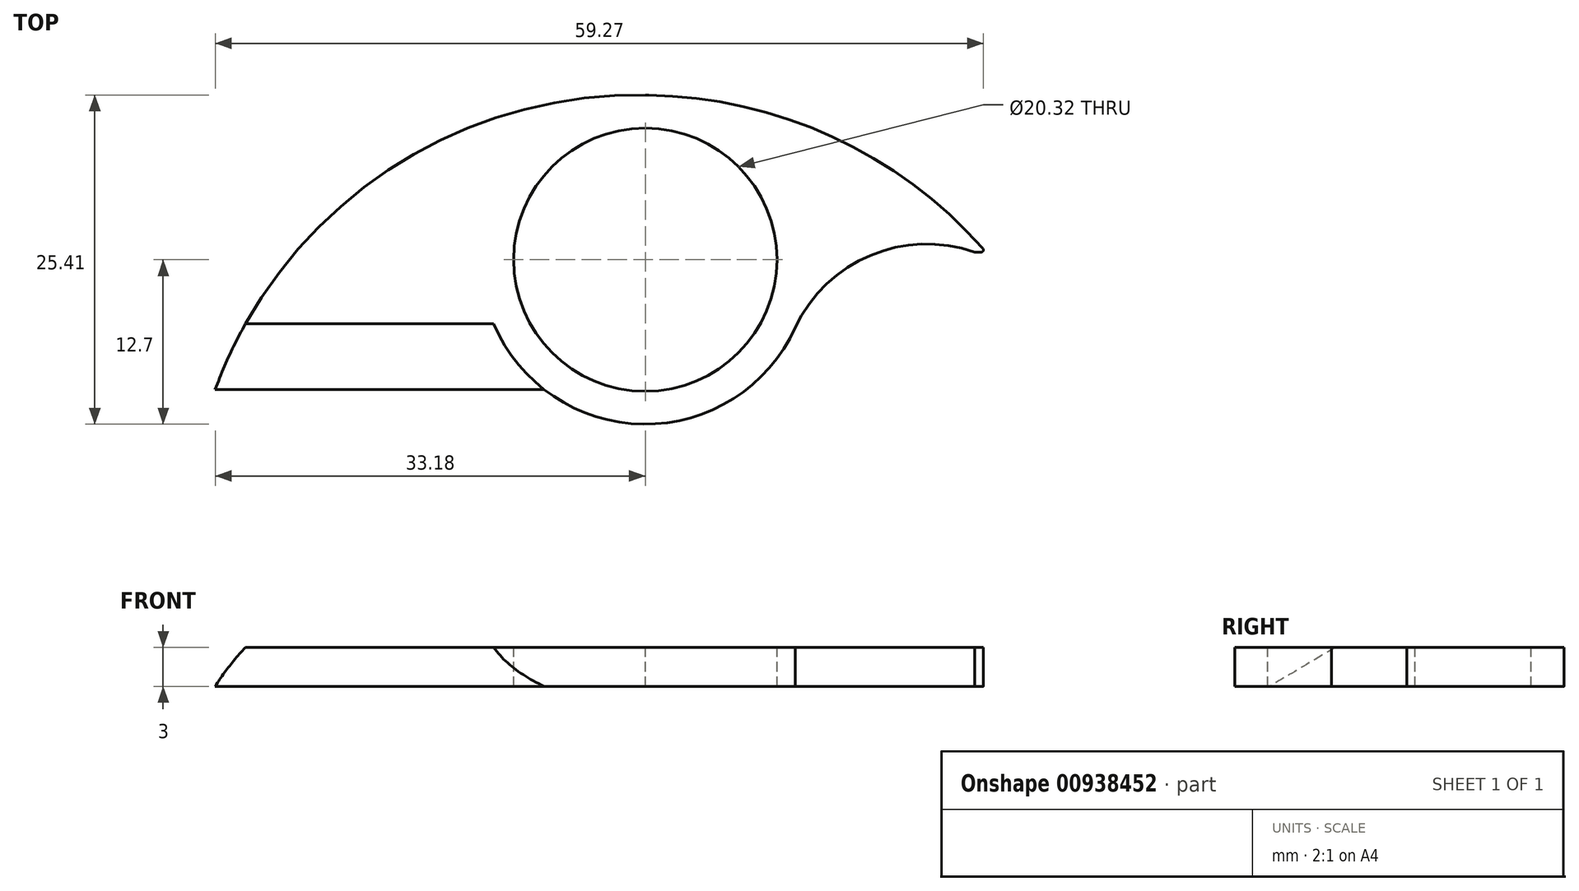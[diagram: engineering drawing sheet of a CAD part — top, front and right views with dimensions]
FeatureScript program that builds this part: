
annotation { "Feature Type Name" : "Feature", "Feature Type Description" : "" }
export const myFeature = defineFeature(function(context is Context, id is Id, definition is map)
    precondition{}
    {
        {
            var Q0;
            Q0=qCreatedBy(makeId("Top.planeOp"),FACE);
            var sketch = newSketch(context, id + "F0", { "sketchPlane" : qUnion([Q0])});
            skCircle(sketch, "E0", {"center": v(0, 0) * mm, "radius": 12.7 * mm});
            skSolve(sketch);
        }
        {
            var Q0;
            Q0 = qSketchRegion(id + "F0", true);
            extrude(context, id + "F1", {"entities" : qUnion([Q0]), "depth" : 3 * mm, "offsetDistance" : 25.4 * mm});
        }
        {
            var Q0;
            Q0=makeQuery(id+"F1.opExtrude","CAP_FACE",FACE,{"disambiguationData":[OSD([sQuery(id+"F0.wireOp",EDGE,"E0")])],"isStart":false});
            var sketch = newSketch(context, id + "F2", { "sketchPlane" : qUnion([Q0])});
            skLineSegment(sketch, "E1", {"start": v(-7.78, -10.04) * mm, "end": v(-33.18, -10.04) * mm});
            skArc(sketch, "E2", {"start": v(0, 12.7) * mm, "mid": v(-20.23, 6.65) * mm, "end": v(-33.18, -10.04) * mm});
            skSolve(sketch);
        }
        {
            var Q0;
            {var subQ0=makeQuery(id+"F1.opExtrude","CAP_EDGE",EDGE,{"disambiguationData":[OSD([sQuery(id+"F0.wireOp",EDGE,"E0")])],"isStart":false});var subQ1=makeQuery(id+"F2.imprint","INTERSECT",VERTEX,{"derivedFrom":[subQ0,sQuery(id+"F2.wireOp",EDGE,"E1")]});Q0=makeQuery(id+"F2.imprint","IMPRINT",FACE,{"disambiguationData":[TD([[makeQuery(id+"F2.imprint","IMPRINT",EDGE,{"disambiguationData":[TD([[subQ1,-1.0]])],"derivedFrom":subQ0}),1.0]])]});}
            var sketch = newSketch(context, id + "F3", { "sketchPlane" : qUnion([Q0])});
            skCircle(sketch, "E3.0", {"center": v(0, 0) * mm, "radius": 10.16 * mm});
            skSolve(sketch);
        }
        {
            var Q0;
            Q0=makeQuery(id+"F3.imprint","IMPRINT",FACE,{"disambiguationData":[TD([[makeQuery(id+"F3.imprint","IMPRINT",EDGE,{"derivedFrom":sQuery(id+"F3.wireOp",EDGE,"E3.0")}),1.0]])]});
            extrude(context, id + "F4", {"entities" : qUnion([Q0]), "operationType" : NewBodyOperationType.REMOVE, "oppositeDirection" : true, "depth" : 18.29 * mm, "offsetDistance" : 25.4 * mm});
        }
        {
            var Q0;
            {var subQ0=sQuery(id+"F2.wireOp",EDGE,"E1");Q0=makeQuery(id+"F2.imprint","IMPRINT",FACE,{"disambiguationData":[TD([[makeQuery(id+"F2.imprint","IMPRINT",EDGE,{"derivedFrom":subQ0}),-1.0]])]});}
            extrude(context, id + "F5", {"entities" : qUnion([Q0]), "operationType" : NewBodyOperationType.ADD, "oppositeDirection" : true, "depth" : 3 * mm, "offsetDistance" : 25.4 * mm});
        }
        {
            var Q0;
            {var subQ0=sQuery(id+"F0.wireOp",EDGE,"E0");Q0=makeQuery(id+"F5.boolean.opBoolean","MERGE",FACE,{"derivedFrom":[makeQuery(id+"F1.opExtrude","CAP_FACE",FACE,{"disambiguationData":[OSD([subQ0])],"isStart":false}),makeQuery(id+"F5.opExtrude","CAP_FACE",FACE,{"disambiguationData":[OSD([subQ0,sQuery(id+"F2.wireOp",EDGE,"E1"),sQuery(id+"F2.wireOp",EDGE,"E2")])],"isStart":true})]});}
            var sketch = newSketch(context, id + "F6", { "sketchPlane" : qUnion([Q0])});
            skArc(sketch, "E4", {"start": v(26.78, 0) * mm, "mid": v(18, 0.58) * mm, "end": v(11.5, -5.37) * mm});
            skArc(sketch, "E5", {"start": v(26.78, 0) * mm, "mid": v(14.8, 9.32) * mm, "end": v(0, 12.7) * mm});
            skSolve(sketch);
        }
        {
            var Q0;
            {var subQ0=sQuery(id+"F6.wireOp",EDGE,"E5");var subQ1=sQuery(id+"F6.wireOp",EDGE,"E4");var subQ2=makeQuery(id+"F6.imprint","INTERSECT",VERTEX,{"derivedFrom":[subQ1,subQ0]});Q0=makeQuery(id+"F6.imprint","IMPRINT",FACE,{"disambiguationData":[TD([[makeQuery(id+"F6.imprint","IMPRINT",EDGE,{"disambiguationData":[TD([[subQ2,-1.0]])],"derivedFrom":subQ1}),-1.0]])]});}
            extrude(context, id + "F7", {"entities" : qUnion([Q0]), "operationType" : NewBodyOperationType.ADD, "oppositeDirection" : true, "depth" : 3 * mm, "offsetDistance" : 25.4 * mm});
        }
        {
            var Q0;
            Q0=makeQuery(id+"F5.opExtrude","CAP_EDGE",EDGE,{"disambiguationData":[OSD([sQuery(id+"F2.wireOp",EDGE,"E1")])],"isStart":true});
            chamfer(context, id + "F8", {"entities" : qUnion([Q0]), "chamferType" : ChamferType.TWO_OFFSETS, "width1" : 3 * mm, "oppositeDirection" : false, "width2" : 5.08 * mm, "tangentPropagation" : true});
        }
        {
            var Q0;
            Q0=makeQuery(id+"F7.opExtrude","SWEPT_EDGE",EDGE,{"disambiguationData":[OSD([sQuery(id+"F6.wireOp",EDGE,"E4"),sQuery(id+"F6.wireOp",EDGE,"E5")])]});
            chamfer(context, id + "F9", {"entities" : qUnion([Q0]), "chamferType" : ChamferType.OFFSET_ANGLE, "width" : 1.5 * mm, "oppositeDirection" : false, "angle" : 30 * degree, "tangentPropagation" : true});
        }
        {
            var Q0;
            {var subQ0=sQuery(id+"F6.wireOp",EDGE,"E5");Q0=makeQuery(id+"F9.opChamfer","BLEND_EDGE",EDGE,{"blendedFrom":[makeQuery(id+"F7.opExtrude","SWEPT_EDGE",EDGE,{"disambiguationData":[OSD([sQuery(id+"F6.wireOp",EDGE,"E4"),subQ0])]}),makeQuery(id+"F7.opExtrude","SWEPT_FACE",FACE,{"disambiguationData":[OSD([subQ0])]})],"blendedInto":[makeQuery(id+"F7.opExtrude","SWEPT_FACE",FACE,{"disambiguationData":[OSD([subQ0])]})]});}
            fillet(context, id + "F10", {"entities" : qUnion([Q0]), "tangentPropagation" : true, "radius" : 0.17 * mm, "defaultsChanged" : true, "vertexSettings" : [], "allowEdgeOverflow" : false});
        }
    });
